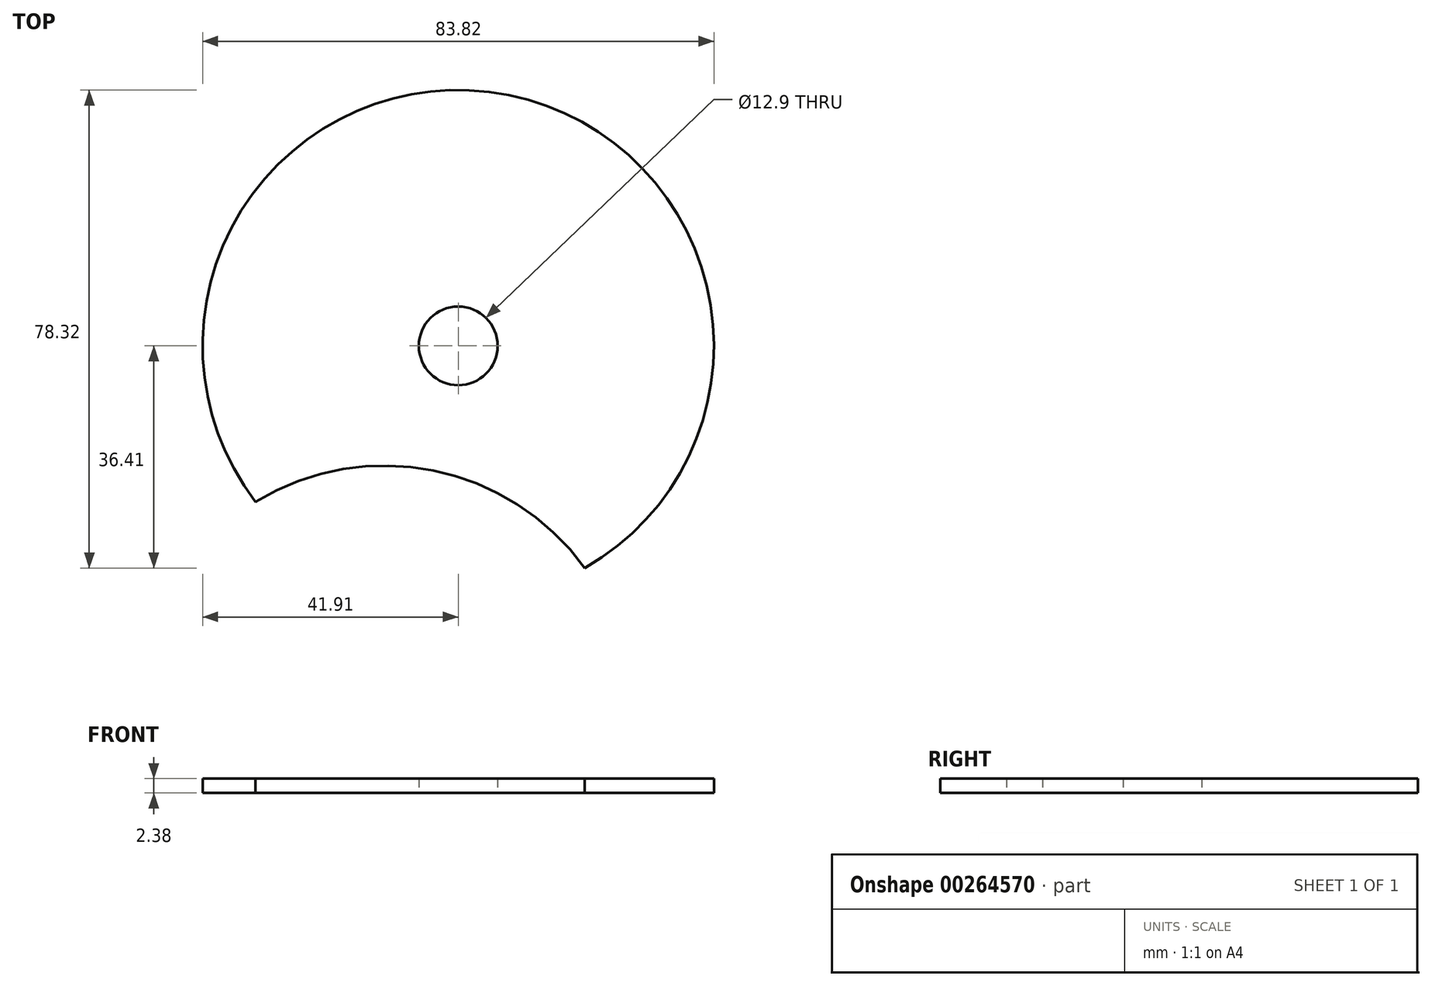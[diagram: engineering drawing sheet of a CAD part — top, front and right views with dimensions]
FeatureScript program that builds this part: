
annotation { "Feature Type Name" : "Feature", "Feature Type Description" : "" }
export const myFeature = defineFeature(function(context is Context, id is Id, definition is map)
    precondition{}
    {
        {
            var Q0;
            Q0=qCreatedBy(makeId("Top.planeOp"),FACE);
            var sketch = newSketch(context, id + "F0", { "sketchPlane" : qUnion([Q0])});
            skArc(sketch, "E0", {"start": v(20.76, -36.4) * mm, "mid": v(8.26, 41.09) * mm, "end": v(-33.22, -25.55) * mm});
            skCircle(sketch, "E1", {"center": v(0, 0) * mm, "radius": 6.45 * mm});
            skArc(sketch, "E2", {"start": v(20.76, -36.4) * mm, "mid": v(-4.11, -20.45) * mm, "end": v(-33.22, -25.55) * mm});
            skSolve(sketch);
        }
        {
            var Q0;
            Q0=makeQuery(id+"F0.imprint","IMPRINT",FACE,{"disambiguationData":[TD([[makeQuery(id+"F0.imprint","IMPRINT",EDGE,{"derivedFrom":sQuery(id+"F0.wireOp",EDGE,"E0")}),1.0]])]});
            extrude(context, id + "F1", {"entities" : qUnion([Q0]), "depth" : 2.38 * mm});
        }
    });
